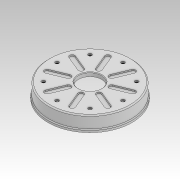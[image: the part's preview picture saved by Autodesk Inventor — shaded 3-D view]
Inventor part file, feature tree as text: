
AUTODESK INVENTOR PART (.ipt)
format: ipt  version: 2022 (Build 260153000, 153)  size: 1,569,792 bytes
history: native  units: mm
features: other x11, extrude x6, sketch x6, pattern_circular x4, chamfer x2, fillet x2, revolve x1, imported_body x1
ambient origin geometry x8: Origin, YZ Plane, XZ Plane, XY Plane, X Axis, Y Axis, Z Axis, Center Point
bodies: Solid1 (feature_tree)
feature tree (33):
  other  "HD_mastersketch.ipt"
  other  "Blocks"
  revolve  "Revolution1"  [1 undecoded]
  extrude  "Extrusion1"  Depth=4.0mm TaperAngle=0.0deg
  extrude  "Extrusion3"  Depth=1.7mm
  pattern_circular  "Circular Pattern1"  Count=73 Angle=360.0deg
  chamfer  "Chamfer1"  Distance=3.2mm
  extrude  "Extrusion2"  Depth=1.0mm
  fillet  "Fillet1"  Radius=4.0mm
  pattern_circular  "Circular Pattern2"  Angle=45.0deg  [1 undecoded]
  extrude  "Extrusion5"  Depth=10.0mm TaperAngle=0.0deg
  fillet  "Fillet2"  Radius=0.5mm
  pattern_circular  "Circular Pattern3"  Count=68 Angle=360.0deg
  extrude  "Extrusion6"  Depth=1.0mm
  chamfer  "Chamfer2"  Distance=22.5mm
  pattern_circular  "Circular Pattern4"  [2 undecoded]
  extrude  "Extrusion7"  Depth=1.0mm TaperAngle=0.0deg
  other  "608 bearing"
  other  "Belt"
  other  "Rotor"
  imported_body  "Base"
  sketch  "Sketch5"  dims[d0=10.0mm d24=7.0mm d25=22.0mm d26=8.0mm]
  sketch  "Sketch6"  dims[d1=90.0deg d4=4.0mm d5=0.0mm]
  sketch  "Sketch7"  dims[d6=80.0mm d7=360.0deg d9=1.7mm]
  other  "M3NutDepth_bot"
  other  "BeltCutDepth_bot"
  other  "M3NutDepth_top"
  other  "BeltCutDepth_top"
  sketch  "Sketch10"  dims[d11=1.25mm]
  sketch  "Sketch11"  dims[d12=4.0mm d13=0.0mm]
  sketch  "Sketch12"  dims[d14=0.5mm d15=730.0mm d16=360.0deg d18=3.2mm d19=5.7mm d20=4.0mm d21=0.0mm d34=0.5mm d35=2.0mm d36=45.0deg d37=0.8mm d38=1.8mm d39=8.726646mm d40=0.523599mm d41=0.523599mm d42=0.523599mm d43=0.523599mm d44=0.523599mm d45=2.792527mm d46=0.523599mm d47=68.0mm d48=70.740362mm d49=1.780032mm d50=9.749343mm d51=7.969311mm d52=6.189278mm d53=4.409246mm d54=2.629213mm d55=0.523599mm d56=0.523599mm d57=0.523599mm d58=0.523599mm d59=0.523599mm d60=11.529376mm d61=13.309408mm d62=15.089441mm d63=16.869473mm d64=18.649506mm d65=0.523599mm d66=0.523599mm d67=20.429538mm d68=22.209571mm d69=0.243598mm d70=72.932651mm d71=10.0mm d72=0.0mm d73=0.5mm d74=680.0mm d75=360.0deg d78=15.0mm d79=22.5mm d80=2.0mm d81=1.0mm d82=0.0mm d83=0.3mm d84=1.0mm d85=45.0deg d86=80.0mm d87=360.0deg d89=10.0mm d90=0.0mm d91=1.0mm d92=0.5mm d93=0.872665mm d94=0.5mm d95=0.872665mm]
  other  "608 bearing:1"
  other  "608 bearing:2"
note: 4 required parameter values undecoded (feature->parameter linkage not recoverable at this tier; creation-order binding heuristic only, values carry confidence <= 0.55)